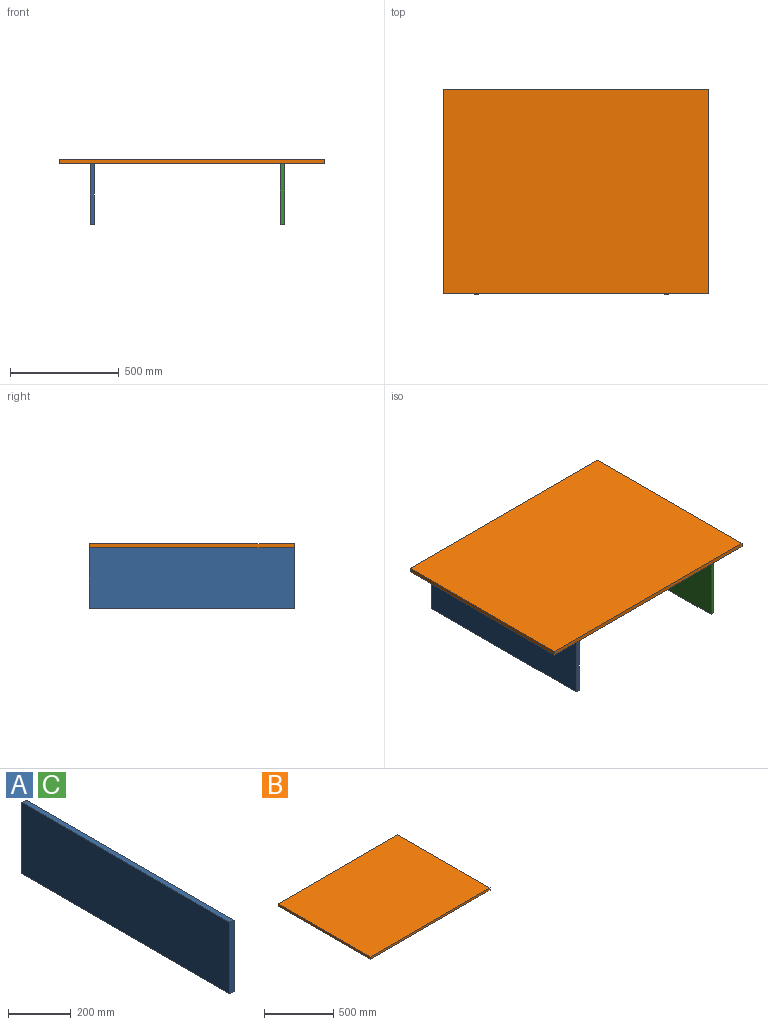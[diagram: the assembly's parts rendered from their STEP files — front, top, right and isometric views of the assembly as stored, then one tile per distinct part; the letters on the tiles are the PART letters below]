
ASSEMBLY  parts=3 mates=1
PART A: 6 faces, bbox 19.1x940x279.2 mm
  f0: plane 939.97x19.05mm, normal (0,0,-1), area 17906.4mm2, adj f1,f3,f4,f5
  f1: plane 279.19x19.05mm, normal (0,1,0), area 5318.6mm2, adj f0,f2,f4,f5
  f2: plane 939.97x19.05mm, normal (0,0,1), area 17906.4mm2, adj f1,f3,f4,f5
  f3: plane 279.19x19.05mm, normal (0,-1,0), area 5318.6mm2, adj f0,f2,f4,f5
  f4: plane 939.97x279.19mm, normal (1,0,0), area 262430.9mm2, adj f0,f1,f2,f3
  f5: plane 939.97x279.19mm, normal (-1,0,0), area 262430.9mm2, adj f0,f1,f2,f3
PART B: 6 faces, bbox 1219.5x938x19.1 mm
  f0: plane 1219.51x19.05mm, normal (0,-1,0), area 23231.6mm2, adj f1,f3,f4,f5
  f1: plane 938.01x19.05mm, normal (1,0,0), area 17869mm2, adj f0,f2,f4,f5
  f2: plane 1219.51x19.05mm, normal (0,1,0), area 23231.6mm2, adj f1,f3,f4,f5
  f3: plane 938.01x19.05mm, normal (-1,0,0), area 17869mm2, adj f0,f2,f4,f5
  f4: plane 1219.51x938.01mm, normal (0,0,1), area 1143906.2mm2, adj f0,f1,f2,f3
  f5: plane 1219.51x938.01mm, normal (0,0,-1), area 1143906.2mm2, adj f0,f1,f2,f3
PART C: same geometry as A
PLACE A t=(-451.04,138.82,28.72)mm
PLACE B t=(16.91,137.84,167.84)mm
PLACE C t=(423.22,136.47,28.52)mm
MATE planar A.f3 <-> B.f0  axis (0,-1,0) through (-441.52,-331.16,28.72)mm
